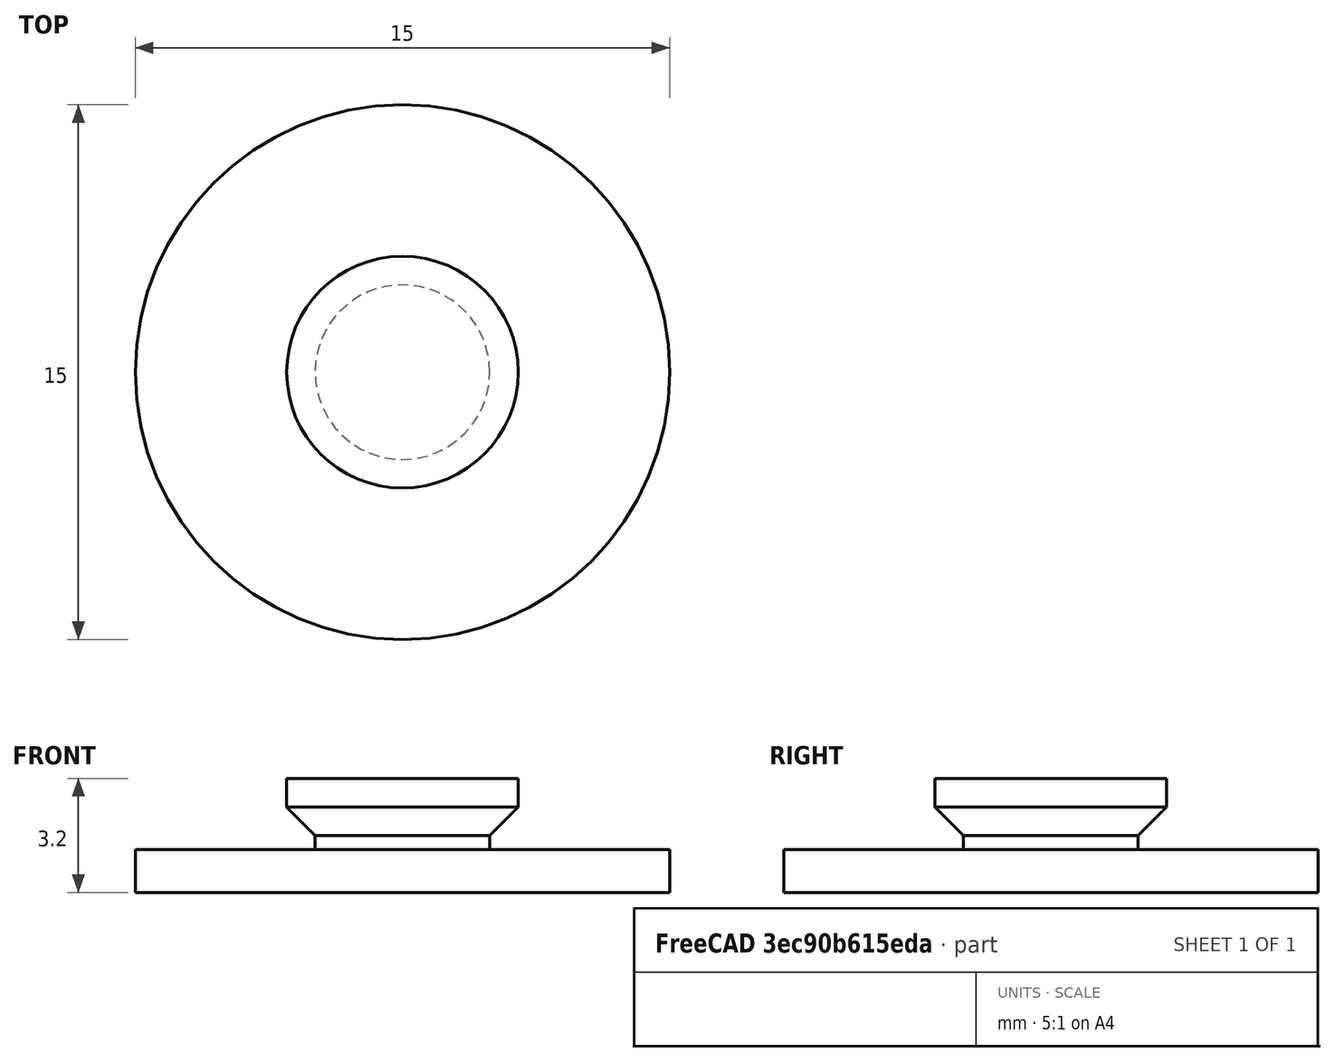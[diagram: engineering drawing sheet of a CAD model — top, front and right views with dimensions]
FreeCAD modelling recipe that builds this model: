
FCSTD DOCUMENT  (FreeCAD 0.19R)
Label: hook_sign_large
License: All rights reserved
LicenseURL: http://en.wikipedia.org/wiki/All_rights_reserved
objects: Sketcher::SketchObject×1, PartDesign::Revolution×1, PartDesign::Body×1
note: 4 computed .brp shape members not serialized (recipe doc carries the construction recipe); baked Part::Feature solids carry a one-line shape summary decoded from their .brp

FEATURE [Sketcher::SketchObject] Sketch
  FullyConstrained = true
  MapMode = 5
  Placement = pos=(0,0,0) rot=(1,0,0;1.5708rad)
  Support = -> [XZ_Plane]
  sketch-geometry (8):
    g0: LineSegment StartX=0 StartY=0 StartZ=0 EndX=-7.5 EndY=0 EndZ=0
    g1: LineSegment StartX=-7.5 StartY=0 StartZ=0 EndX=-7.5 EndY=1.2 EndZ=0
    g2: LineSegment StartX=-7.5 StartY=1.2 StartZ=0 EndX=-2.45 EndY=1.2 EndZ=0
    g3: LineSegment StartX=-2.45 StartY=1.2 StartZ=0 EndX=-2.45 EndY=1.6 EndZ=0
    g4: LineSegment StartX=-2.45 StartY=1.6 StartZ=0 EndX=-3.25 EndY=2.4 EndZ=0
    g5: LineSegment StartX=-3.25 StartY=2.4 StartZ=0 EndX=-3.25 EndY=3.2 EndZ=0
    g6: LineSegment StartX=-3.25 StartY=3.2 StartZ=0 EndX=0 EndY=3.2 EndZ=0
    g7: LineSegment StartX=0 StartY=3.2 StartZ=0 EndX=0 EndY=0 EndZ=0
  constraints (23):
    c: Coincident(g-1,g0)
    c: Horizontal(g0)
    c: Coincident(g0,g1)
    c: Vertical(g1)
    c: Coincident(g1,g2)
    c: Horizontal(g2)
    c: Coincident(g2,g3)
    c: Vertical(g3)
    c: Coincident(g3,g4)
    c: Coincident(g4,g5)
    c: Vertical(g5)
    c: Coincident(g5,g6)
    c: Horizontal(g6)
    c: Coincident(g6,g7)
    c: Coincident(g7,g0)
    c: Vertical(g7)
    c: DistanceX(g0,g0) = 7.5
    c: DistanceY(g1,g1) = 1.2
    c: DistanceX(g6,g6) = 3.25
    c: DistanceX(g4,g4) = 0.8
    c: DistanceY(g5,g5) = 0.8
    c: DistanceY(g2,g4) = 1.2
    c: DistanceY(g3,g3) = 0.4
FEATURE [PartDesign::Revolution] Revolution
  Angle = 360
  Axis = (0,2e-16,1)
  Base = (0,0,0)
  Placement = pos=(0,0,0) rot=(1,0,0;1.5708rad)
  Profile = -> Sketch
  ReferenceAxis = -> Sketch [V_Axis]
  Refine = true
FEATURE [PartDesign::Body] Body
  Group = -> [Sketch,Revolution]
  Origin = -> Origin
  Tip = -> Revolution
